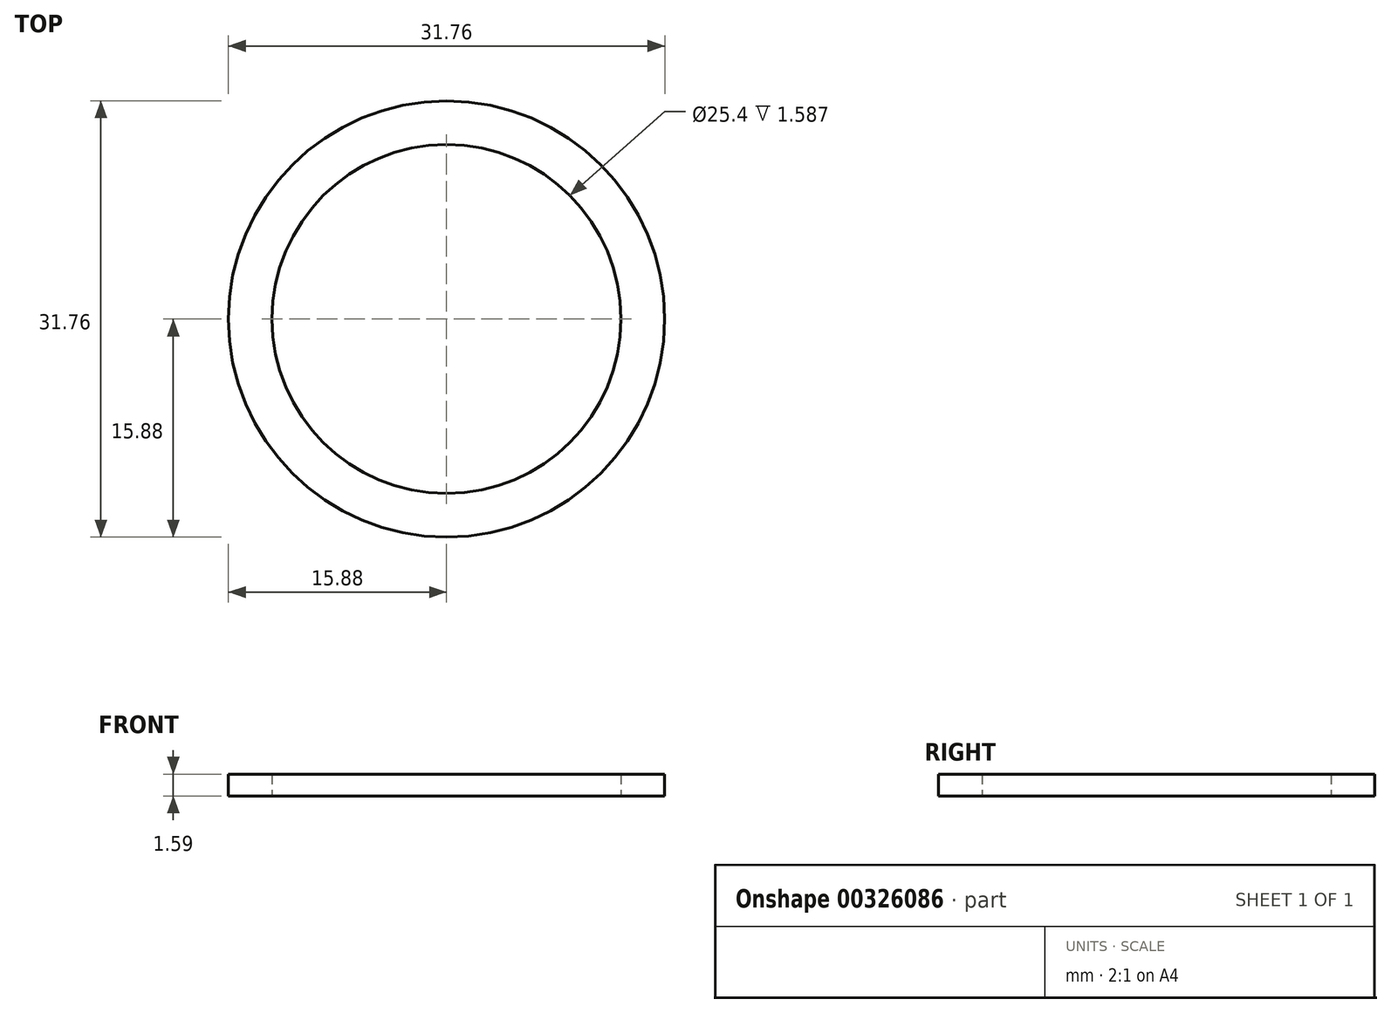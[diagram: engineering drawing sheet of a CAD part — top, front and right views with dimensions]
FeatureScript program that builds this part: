
annotation { "Feature Type Name" : "Feature", "Feature Type Description" : "" }
export const myFeature = defineFeature(function(context is Context, id is Id, definition is map)
    precondition{}
    {
        {
            var Q0;
            Q0=qCreatedBy(makeId("Top.planeOp"),FACE);
            var sketch = newSketch(context, id + "F0", { "sketchPlane" : qUnion([Q0])});
            skCircle(sketch, "E0", {"center": v(0, 0) * mm, "radius": 12.7 * mm});
            skCircle(sketch, "E1", {"center": v(0, 0) * mm, "radius": 15.88 * mm});
            skSolve(sketch);
        }
        {
            var Q0;
            Q0 = qSketchRegion(id + "F0", true);
            extrude(context, id + "F1", {"entities" : qUnion([Q0]), "depth" : 1.59 * mm});
        }
    });
